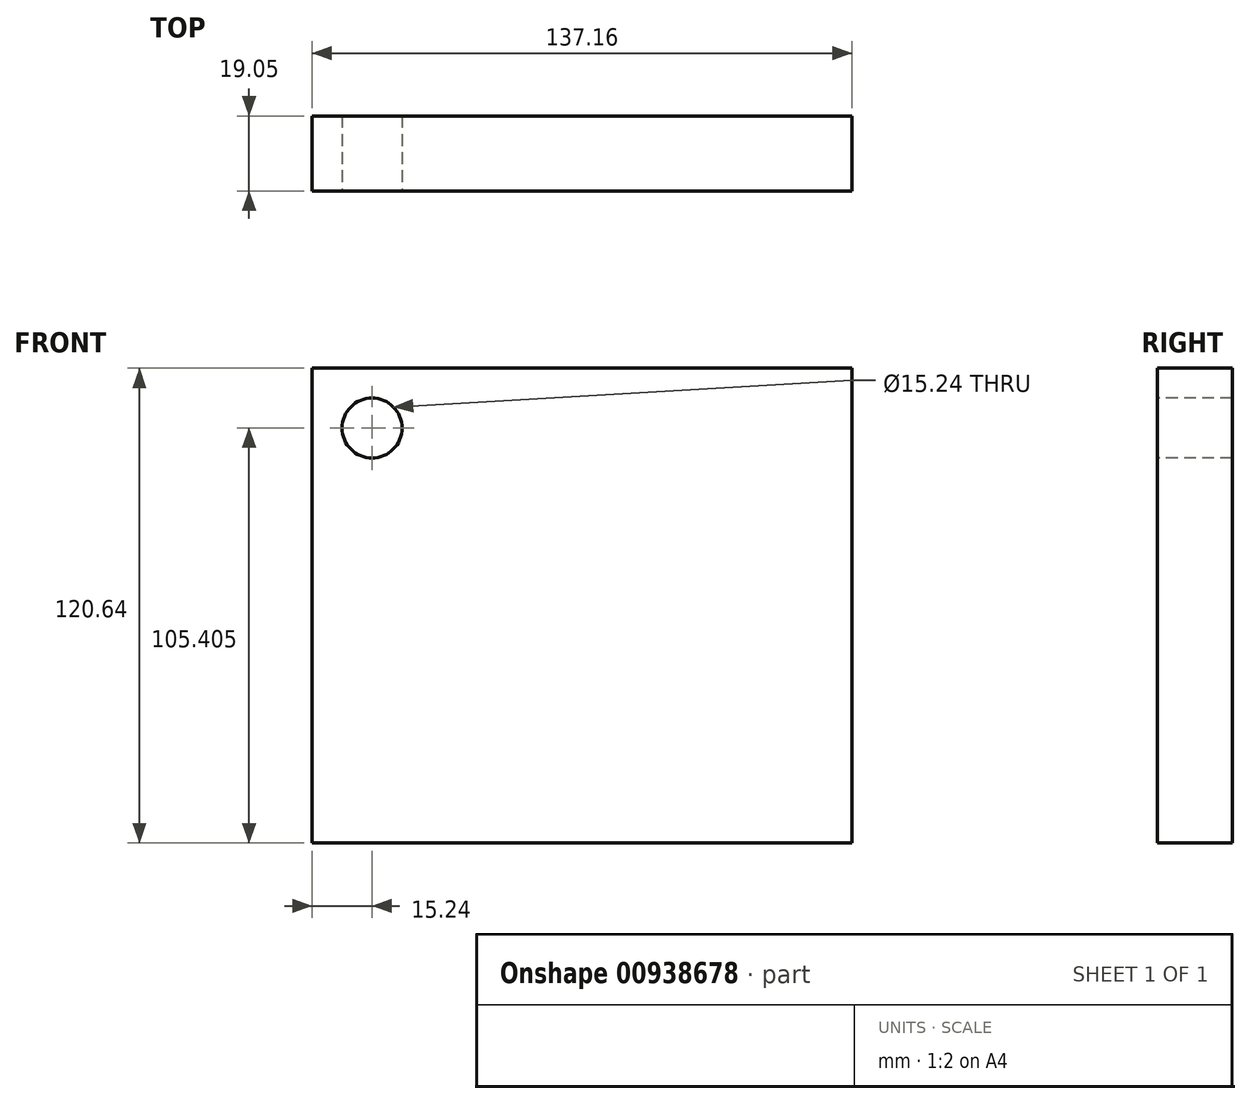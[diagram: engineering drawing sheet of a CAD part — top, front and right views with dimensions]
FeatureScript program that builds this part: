
annotation { "Feature Type Name" : "Feature", "Feature Type Description" : "" }
export const myFeature = defineFeature(function(context is Context, id is Id, definition is map)
    precondition{}
    {
        {
            var Q0;
            Q0=qCreatedBy(makeId("Front.planeOp"),FACE);
            var sketch = newSketch(context, id + "F0", { "sketchPlane" : qUnion([Q0])});
            skLineSegment(sketch, "E0.bottom", {"start": v(68.58, 60.33) * mm, "end": v(-68.58, 60.33) * mm});
            skLineSegment(sketch, "E0.top", {"start": v(68.58, -60.33) * mm, "end": v(-68.58, -60.33) * mm});
            skLineSegment(sketch, "E0.left", {"start": v(68.58, 60.33) * mm, "end": v(68.58, -60.33) * mm});
            skLineSegment(sketch, "E0.right", {"start": v(-68.58, 60.33) * mm, "end": v(-68.58, -60.33) * mm});
            skPoint(sketch, "E0.middle", {"position": v(0, 0) * mm});
            skSolve(sketch);
        }
        {
            var Q0;
            Q0=qSketchRegion(id+"F0",true);
            extrude(context, id + "F1", {"entities" : qUnion([Q0]), "depth" : 19.05 * mm, "offsetDistance" : 25.4 * mm});
        }
        {
            var Q0;
            Q0=makeQuery(id+"F1.opExtrude","CAP_FACE",FACE,{"disambiguationData":[OSD([sQuery(id+"F0.wireOp",EDGE,"E0.bottom"),sQuery(id+"F0.wireOp",EDGE,"E0.top"),sQuery(id+"F0.wireOp",EDGE,"E0.left"),sQuery(id+"F0.wireOp",EDGE,"E0.right")])],"isStart":false});
            var sketch = newSketch(context, id + "F2", { "sketchPlane" : qUnion([Q0])});
            skCircle(sketch, "E1", {"center": v(-53.34, 45.09) * mm, "radius": 7.62 * mm});
            skLineSegment(sketch, "E2", {"start": v(-53.34, 45.09) * mm, "end": v(-53.34, 60.33) * mm, "construction": true});
            skLineSegment(sketch, "E3", {"start": v(-53.34, 45.09) * mm, "end": v(-68.58, 45.09) * mm, "construction": true});
            skSolve(sketch);
        }
        {
            var Q0;
            Q0=qSketchRegion(id+"F2",true);
            extrude(context, id + "F3", {"entities" : qUnion([Q0]), "operationType" : NewBodyOperationType.REMOVE, "endBound" : BoundingType.THROUGH_ALL, "oppositeDirection" : true, "depth" : 25.4 * mm, "offsetDistance" : 25.4 * mm});
        }
    });
